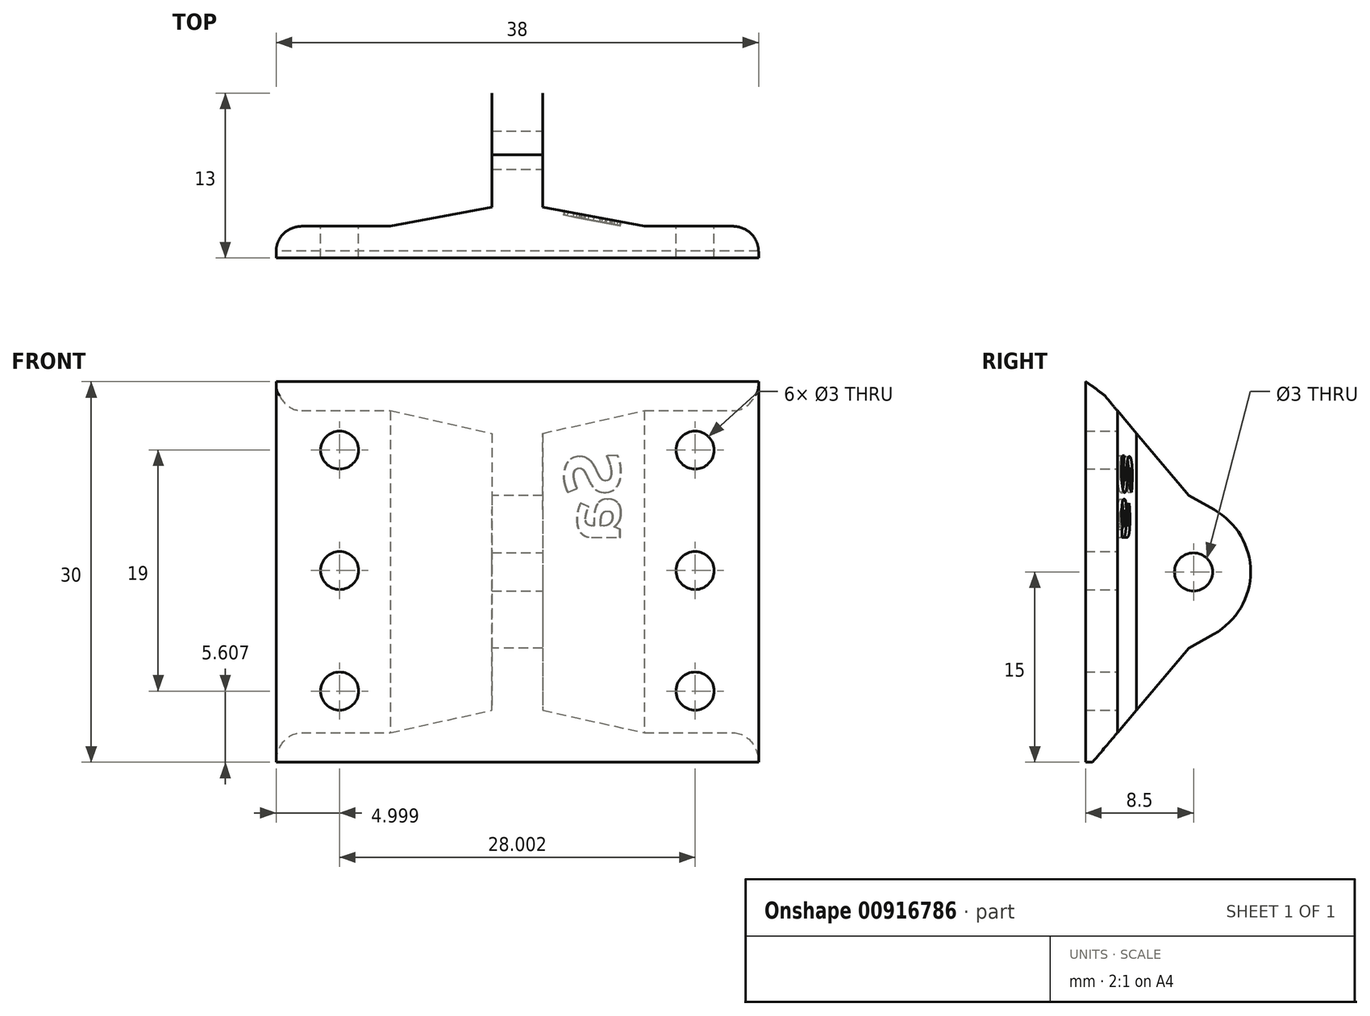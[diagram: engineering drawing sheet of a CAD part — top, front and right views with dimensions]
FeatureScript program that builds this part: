
annotation { "Feature Type Name" : "Feature", "Feature Type Description" : "" }
export const myFeature = defineFeature(function(context is Context, id is Id, definition is map)
    precondition{}
    {
        {
            var Q0;
            Q0=qCreatedBy(makeId("Top.planeOp"),FACE);
            var sketch = newSketch(context, id + "F0", { "sketchPlane" : qUnion([Q0])});
            skLineSegment(sketch, "E0", {"start": v(0, 0) * mm, "end": v(38, 0) * mm});
            skLineSegment(sketch, "E1", {"start": v(38, 0) * mm, "end": v(38, 2.5) * mm});
            skLineSegment(sketch, "E2", {"start": v(21, 4) * mm, "end": v(21, 13) * mm});
            skLineSegment(sketch, "E3", {"start": v(21, 13) * mm, "end": v(17, 13) * mm});
            skLineSegment(sketch, "E4", {"start": v(0, 2.5) * mm, "end": v(0, 0) * mm});
            skLineSegment(sketch, "E5", {"start": v(17, 13) * mm, "end": v(17, 4) * mm});
            skLineSegment(sketch, "E6", {"start": v(17, 4) * mm, "end": v(9, 2.5) * mm});
            skLineSegment(sketch, "E7", {"start": v(9, 2.5) * mm, "end": v(0, 2.5) * mm});
            skLineSegment(sketch, "E8", {"start": v(38, 2.5) * mm, "end": v(29, 2.5) * mm});
            skLineSegment(sketch, "E9", {"start": v(29, 2.5) * mm, "end": v(21, 4) * mm});
            skLineSegment(sketch, "E10", {"start": v(17, 4) * mm, "end": v(21, 4) * mm});
            skSolve(sketch);
        }
        {
            var Q0;
            Q0 = qSketchRegion(id + "F0", true);
            var Q1;
            Q1 = qSketchRegion(id + "F2", true);
            extrude(context, id + "F1", {"entities" : qUnion([Q0, Q1]), "depth" : 30 * mm, "offsetDistance" : 25 * mm});
        }
        {
            var Q0;
            Q0=qCreatedBy(makeId("Right.planeOp"),FACE);
            var sketch = newSketch(context, id + "F2", { "sketchPlane" : qUnion([Q0])});
            skLineSegment(sketch, "E11", {"start": v(14, 17.73) * mm, "end": v(8.13, 21.02) * mm});
            skLineSegment(sketch, "E12", {"start": v(8.13, 21.02) * mm, "end": v(0.55, 30.03) * mm});
            skLineSegment(sketch, "E13", {"start": v(14, 12.28) * mm, "end": v(8.13, 9) * mm});
            skLineSegment(sketch, "E14", {"start": v(8.13, 9) * mm, "end": v(0.55, 0) * mm});
            skLineSegment(sketch, "E15", {"start": v(0.55, 0) * mm, "end": v(14, 0) * mm});
            skLineSegment(sketch, "E16", {"start": v(14, 0) * mm, "end": v(14, 12.28) * mm});
            skLineSegment(sketch, "E17", {"start": v(14, 17.73) * mm, "end": v(14, 30) * mm});
            skLineSegment(sketch, "E18", {"start": v(14, 30) * mm, "end": v(0.55, 30.03) * mm});
            skSolve(sketch);
        }
        {
            var Q0;
            Q0=makeQuery(id+"F1.opExtrude","SWEPT_FACE",FACE,{"disambiguationData":[OSD([sQuery(id+"F0.wireOp",EDGE,"E5")])]});
            var sketch = newSketch(context, id + "F3", { "sketchPlane" : qUnion([Q0])});
            skPoint(sketch, "E19", {"position": v(-8.5, 15) * mm});
            skPoint(sketch, "E19.positionSnap0", {"position": v(-8.5, 0) * mm});
            skPoint(sketch, "E19.positionSnap1", {"position": v(-4, 15) * mm});
            skSolve(sketch);
        }
        {
            var Q0;
            Q0 = qSketchRegion(id + "F2", true);
            extrude(context, id + "F4", {"entities" : qUnion([Q0]), "operationType" : NewBodyOperationType.REMOVE, "depth" : 39 * mm, "offsetDistance" : 25 * mm});
        }
        {
            var Q0;
            Q0=sQuery(id+"F3.wireOp",VERTEX,"E19");
            var Q1;
            Q1=makeQuery(id+"F1.opExtrude","SWEPT_BODY",BODY,{"disambiguationData":[OSD([sQuery(id+"F0.wireOp",EDGE,"E0"),sQuery(id+"F0.wireOp",EDGE,"E1"),sQuery(id+"F0.wireOp",EDGE,"E2"),sQuery(id+"F0.wireOp",EDGE,"E3"),sQuery(id+"F0.wireOp",EDGE,"E4"),sQuery(id+"F0.wireOp",EDGE,"E5"),sQuery(id+"F0.wireOp",EDGE,"E6"),sQuery(id+"F0.wireOp",EDGE,"E7"),sQuery(id+"F0.wireOp",EDGE,"E8"),sQuery(id+"F0.wireOp",EDGE,"E9")])]});
            hole(context, id + "F5", {"style" : HoleStyle.SIMPLE, "endStyle" : HoleEndStyle.THROUGH, "holeDiameter" : 3 * mm, "majorDiameter" : 5 * mm, "isTappedThrough" : true, "tappedDepth" : 12 * mm, "tapClearance" : 3, "locations" : qUnion([Q0]), "scope" : qUnion([Q1]), "startStyle" : HoleStartStyle.PART});
        }
        {
            var Q0;
            Q0=makeQuery(id+"F4.boolean.opBoolean","COPY",EDGE,{"derivedFrom":makeQuery(id+"F4.opExtrude","SWEPT_EDGE",EDGE,{"disambiguationData":[OSD([sQuery(id+"F2.wireOp",EDGE,"E14"),sQuery(id+"F2.wireOp",EDGE,"E15")])]})});
            var Q1;
            Q1=makeQuery(id+"F4.boolean.opBoolean","INTERSECT",EDGE,{"derivedFrom":[makeQuery(id+"F1.opExtrude","CAP_FACE",FACE,{"disambiguationData":[OSD([sQuery(id+"F0.wireOp",EDGE,"E0"),sQuery(id+"F0.wireOp",EDGE,"E1"),sQuery(id+"F0.wireOp",EDGE,"E2"),sQuery(id+"F0.wireOp",EDGE,"E3"),sQuery(id+"F0.wireOp",EDGE,"E4"),sQuery(id+"F0.wireOp",EDGE,"E5"),sQuery(id+"F0.wireOp",EDGE,"E6"),sQuery(id+"F0.wireOp",EDGE,"E7"),sQuery(id+"F0.wireOp",EDGE,"E8"),sQuery(id+"F0.wireOp",EDGE,"E9")])],"isStart":false}),makeQuery(id+"F4.opExtrude","SWEPT_FACE",FACE,{"disambiguationData":[OSD([sQuery(id+"F2.wireOp",EDGE,"E12")])]})]});
            fillet(context, id + "F6", {"entities" : qUnion([Q0, Q1]), "radius" : 4 * mm, "tangentPropagation" : true, "rho" : 0.1, "crossSection" : FilletCrossSection.CONIC, "allowEdgeOverflow" : false});
        }
        {
            var Q0;
            Q0=makeQuery(id+"F1.opExtrude","SWEPT_EDGE",EDGE,{"disambiguationData":[OSD([sQuery(id+"F0.wireOp",EDGE,"E4"),sQuery(id+"F0.wireOp",EDGE,"E7")])]});
            var Q1;
            Q1=makeQuery(id+"F1.opExtrude","SWEPT_EDGE",EDGE,{"disambiguationData":[OSD([sQuery(id+"F0.wireOp",EDGE,"E1"),sQuery(id+"F0.wireOp",EDGE,"E8")])]});
            fillet(context, id + "F7", {"entities" : qUnion([Q0, Q1]), "radius" : 2 * mm, "tangentPropagation" : true, "allowEdgeOverflow" : false});
        }
        {
            var Q0;
            Q0=qCreatedBy(makeId("Front.planeOp"),FACE);
            var sketch = newSketch(context, id + "F8", { "sketchPlane" : qUnion([Q0])});
            skPoint(sketch, "E20", {"position": v(33, 24.6) * mm});
            skPoint(sketch, "E21", {"position": v(33, 15.1) * mm});
            skPoint(sketch, "E22", {"position": v(33, 5.6) * mm});
            skPoint(sketch, "E23", {"position": v(5, 5.6) * mm});
            skPoint(sketch, "E24", {"position": v(5, 15.1) * mm});
            skPoint(sketch, "E25", {"position": v(5, 24.6) * mm});
            skSolve(sketch);
        }
        {
            var Q0;
            Q0=sQuery(id+"F8.wireOp",VERTEX,"E20");
            var Q1;
            Q1=sQuery(id+"F8.wireOp",VERTEX,"E21");
            var Q2;
            Q2=sQuery(id+"F8.wireOp",VERTEX,"E22");
            var Q3;
            Q3=sQuery(id+"F8.wireOp",VERTEX,"E25");
            var Q4;
            Q4=sQuery(id+"F8.wireOp",VERTEX,"E24");
            var Q5;
            Q5=sQuery(id+"F8.wireOp",VERTEX,"E23");
            var Q6;
            Q6=makeQuery(id+"F1.opExtrude","SWEPT_BODY",BODY,{"disambiguationData":[OSD([sQuery(id+"F0.wireOp",EDGE,"E0"),sQuery(id+"F0.wireOp",EDGE,"E1"),sQuery(id+"F0.wireOp",EDGE,"E2"),sQuery(id+"F0.wireOp",EDGE,"E3"),sQuery(id+"F0.wireOp",EDGE,"E4"),sQuery(id+"F0.wireOp",EDGE,"E5"),sQuery(id+"F0.wireOp",EDGE,"E6"),sQuery(id+"F0.wireOp",EDGE,"E7"),sQuery(id+"F0.wireOp",EDGE,"E8"),sQuery(id+"F0.wireOp",EDGE,"E9")])]});
            hole(context, id + "F9", {"style" : HoleStyle.SIMPLE, "endStyle" : HoleEndStyle.THROUGH, "holeDiameter" : 3 * mm, "majorDiameter" : 5 * mm, "isTappedThrough" : true, "tappedDepth" : 12 * mm, "tapClearance" : 3, "locations" : qUnion([Q0, Q1, Q2, Q3, Q4, Q5]), "scope" : qUnion([Q6]), "startStyle" : HoleStartStyle.PART});
        }
        {
            var Q0;
            Q0=makeQuery(id+"F1.opExtrude","SWEPT_FACE",FACE,{"disambiguationData":[OSD([sQuery(id+"F0.wireOp",EDGE,"E9")])]});
            var sketch = newSketch(context, id + "F10", { "sketchPlane" : qUnion([Q0])});
            skText(sketch, "E26", { "text": "Sa", "fontName": "OpenSans-Bold.ttf"});
            const initialGuessF10  = {"E26": [-0.02614, 0.02444, 0, -1, 0.00448]};
            skSetInitialGuess(sketch, initialGuessF10);
            skSolve(sketch);
        }
        {
            var Q0;
            Q0 = qSketchRegion(id + "F10", true);
            extrude(context, id + "F11", {"entities" : qUnion([Q0]), "operationType" : NewBodyOperationType.REMOVE, "oppositeDirection" : true, "depth" : 0.3 * mm, "offsetDistance" : 25 * mm});
        }
        {
            var Q0;
            Q0=makeQuery(id+"F4.boolean.opBoolean","INTERSECT",EDGE,{"derivedFrom":[makeQuery(id+"F1.opExtrude","SWEPT_FACE",FACE,{"disambiguationData":[OSD([sQuery(id+"F0.wireOp",EDGE,"E3")])]}),makeQuery(id+"F4.opExtrude","SWEPT_FACE",FACE,{"disambiguationData":[OSD([sQuery(id+"F2.wireOp",EDGE,"E11")])]})]});
            var Q1;
            Q1=makeQuery(id+"F4.boolean.opBoolean","INTERSECT",EDGE,{"derivedFrom":[makeQuery(id+"F1.opExtrude","SWEPT_FACE",FACE,{"disambiguationData":[OSD([sQuery(id+"F0.wireOp",EDGE,"E3")])]}),makeQuery(id+"F4.opExtrude","SWEPT_FACE",FACE,{"disambiguationData":[OSD([sQuery(id+"F2.wireOp",EDGE,"E13")])]})]});
            fillet(context, id + "F12", {"entities" : qUnion([Q0, Q1]), "radius" : 5.63 * mm, "tangentPropagation" : true, "allowEdgeOverflow" : false});
        }
    });
